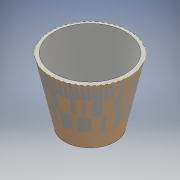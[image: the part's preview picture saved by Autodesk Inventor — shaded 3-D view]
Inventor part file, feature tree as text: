
AUTODESK INVENTOR PART (.ipt)
format: ipt  version: 2016 (Build 200138000, 138)  size: 122,368 bytes
history: native  units: mm
features: sketch x2, plane x1, thicken_offset x1, other x1, loft x1
ambient origin geometry x8: Origin, YZ Plane, XZ Plane, XY Plane, X Axis, Y Axis, Z Axis, Center Point
bodies: Body1 (feature_tree), Body2 (feature_tree)
feature tree (6):
  sketch  "Sketch1"  dims[d0=219.0mm d1=9.52mm]
  plane  "Work Plane1"
  thicken_offset  "Thicken1"
  sketch  "Sketch2"  dims[d2=-178.0mm d3=141.0mm d4=9.52mm d15=0.0mm d16=90.0deg d17=0.0mm d18=90.0deg d19=9.52mm d20=9.52mm]
  other  "Srf1"
  loft  "LoftSrf1"
